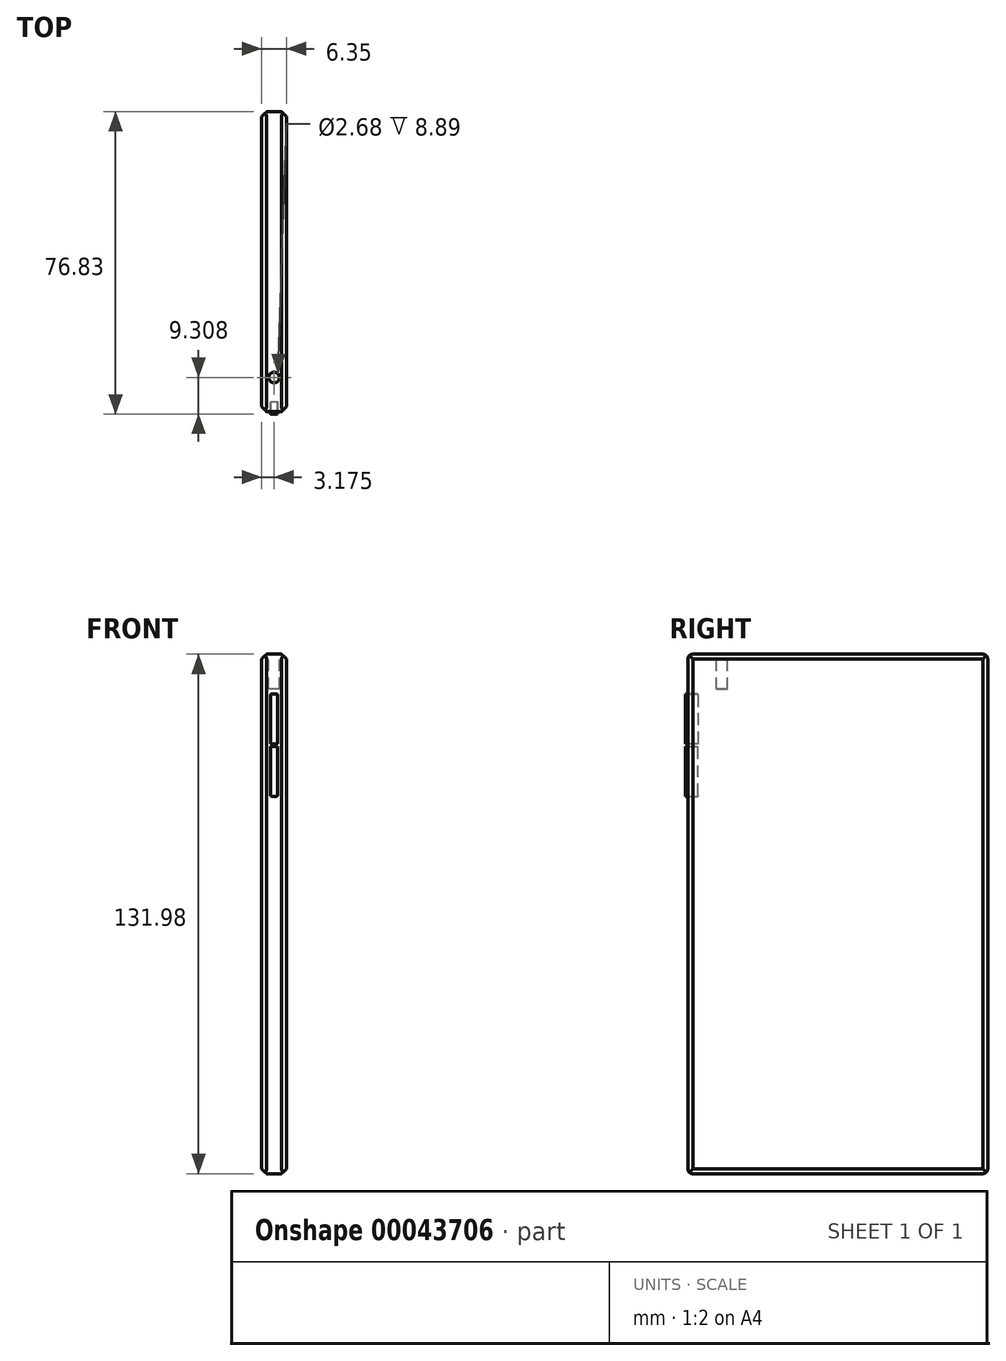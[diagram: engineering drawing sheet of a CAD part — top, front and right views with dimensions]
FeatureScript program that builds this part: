
annotation { "Feature Type Name" : "Feature", "Feature Type Description" : "" }
export const myFeature = defineFeature(function(context is Context, id is Id, definition is map)
    precondition{}
    {
        {
            var Q0;
            Q0=qCreatedBy(makeId("Right.planeOp"),FACE);
            var sketch = newSketch(context, id + "F0", { "sketchPlane" : qUnion([Q0])});
            skLineSegment(sketch, "E0.bottom", {"start": v(-38.1, -63.9) * mm, "end": v(38.1, -63.9) * mm});
            skLineSegment(sketch, "E0.top", {"start": v(-38.1, 68.08) * mm, "end": v(38.1, 68.08) * mm});
            skLineSegment(sketch, "E0.left", {"start": v(-38.1, -63.9) * mm, "end": v(-38.1, 68.08) * mm});
            skLineSegment(sketch, "E0.right", {"start": v(38.1, -63.9) * mm, "end": v(38.1, 68.08) * mm});
            skSolve(sketch);
        }
        {
            var Q0;
            Q0 = qSketchRegion(id + "F0", true);
            extrude(context, id + "F1", {"entities" : qUnion([Q0]), "depth" : 6.35 * mm});
        }
        {
            var Q0;
            Q0=makeQuery(id+"F1.opExtrude","CAP_FACE",FACE,{"disambiguationData":[OSD([sQuery(id+"F0.wireOp",EDGE,"E0.bottom"),sQuery(id+"F0.wireOp",EDGE,"E0.top"),sQuery(id+"F0.wireOp",EDGE,"E0.left"),sQuery(id+"F0.wireOp",EDGE,"E0.right")])],"isStart":false});
            var sketch = newSketch(context, id + "F2", { "sketchPlane" : qUnion([Q0])});
            skSolve(sketch);
        }
        {
            var Q0;
            Q0=makeQuery(id+"F1.opExtrude","CAP_EDGE",EDGE,{"disambiguationData":[OSD([sQuery(id+"F0.wireOp",EDGE,"E0.right")])],"isStart":false});
            var Q1;
            Q1=makeQuery(id+"F1.opExtrude","CAP_EDGE",EDGE,{"disambiguationData":[OSD([sQuery(id+"F0.wireOp",EDGE,"E0.right")])],"isStart":true});
            var Q2;
            Q2=makeQuery(id+"F1.opExtrude","CAP_EDGE",EDGE,{"disambiguationData":[OSD([sQuery(id+"F0.wireOp",EDGE,"E0.bottom")])],"isStart":false});
            var Q3;
            Q3=makeQuery(id+"F1.opExtrude","CAP_EDGE",EDGE,{"disambiguationData":[OSD([sQuery(id+"F0.wireOp",EDGE,"E0.bottom")])],"isStart":true});
            var Q4;
            Q4=makeQuery(id+"F1.opExtrude","CAP_EDGE",EDGE,{"disambiguationData":[OSD([sQuery(id+"F0.wireOp",EDGE,"E0.left")])],"isStart":false});
            var Q5;
            Q5=makeQuery(id+"F1.opExtrude","CAP_EDGE",EDGE,{"disambiguationData":[OSD([sQuery(id+"F0.wireOp",EDGE,"E0.left")])],"isStart":true});
            var Q6;
            Q6=makeQuery(id+"F1.opExtrude","CAP_EDGE",EDGE,{"disambiguationData":[OSD([sQuery(id+"F0.wireOp",EDGE,"E0.top")])],"isStart":false});
            var Q7;
            Q7=makeQuery(id+"F1.opExtrude","CAP_EDGE",EDGE,{"disambiguationData":[OSD([sQuery(id+"F0.wireOp",EDGE,"E0.top")])],"isStart":true});
            chamfer(context, id + "F3", {"entities" : qUnion([Q0, Q1, Q2, Q3, Q4, Q5, Q6, Q7]), "width" : 1.27 * mm, "tangentPropagation" : true});
        }
        {
            var Q0;
            Q0=makeQuery(id+"F1.opExtrude","SWEPT_EDGE",EDGE,{"disambiguationData":[OSD([sQuery(id+"F0.wireOp",EDGE,"E0.top"),sQuery(id+"F0.wireOp",EDGE,"E0.left")])]});
            var Q1;
            Q1=makeQuery(id+"F1.opExtrude","SWEPT_EDGE",EDGE,{"disambiguationData":[OSD([sQuery(id+"F0.wireOp",EDGE,"E0.bottom"),sQuery(id+"F0.wireOp",EDGE,"E0.left")])]});
            var Q2;
            Q2=makeQuery(id+"F1.opExtrude","SWEPT_EDGE",EDGE,{"disambiguationData":[OSD([sQuery(id+"F0.wireOp",EDGE,"E0.top"),sQuery(id+"F0.wireOp",EDGE,"E0.right")])]});
            var Q3;
            Q3=makeQuery(id+"F1.opExtrude","SWEPT_EDGE",EDGE,{"disambiguationData":[OSD([sQuery(id+"F0.wireOp",EDGE,"E0.bottom"),sQuery(id+"F0.wireOp",EDGE,"E0.right")])]});
            fillet(context, id + "F4", {"entities" : qUnion([Q0, Q1, Q2, Q3]), "radius" : 1.27 * mm, "tangentPropagation" : true, "allowEdgeOverflow" : false});
        }
        {
            var Q0;
            Q0=makeQuery(id+"F1.opExtrude","SWEPT_FACE",FACE,{"disambiguationData":[OSD([sQuery(id+"F0.wireOp",EDGE,"E0.left")])]});
            var sketch = newSketch(context, id + "F5", { "sketchPlane" : qUnion([Q0])});
            skLineSegment(sketch, "E1.bottom", {"start": v(2.54, 57.96) * mm, "end": v(3.8, 57.96) * mm});
            skLineSegment(sketch, "E1.top", {"start": v(2.54, 45.26) * mm, "end": v(3.81, 45.26) * mm});
            skLineSegment(sketch, "E1.left", {"start": v(2.29, 57.7) * mm, "end": v(2.29, 45.52) * mm});
            skLineSegment(sketch, "E1.right", {"start": v(4.06, 57.7) * mm, "end": v(4.06, 45.52) * mm});
            skLineSegment(sketch, "E2.MirrorCS", {"start": v(2.54, 44.68) * mm, "end": v(3.81, 44.68) * mm});
            skLineSegment(sketch, "E3.MirrorCS", {"start": v(2.29, 32.25) * mm, "end": v(2.29, 44.43) * mm});
            skLineSegment(sketch, "E4.MirrorCS", {"start": v(4.06, 32.25) * mm, "end": v(4.06, 44.43) * mm});
            skLineSegment(sketch, "E5.MirrorCS", {"start": v(2.54, 32) * mm, "end": v(3.8, 32) * mm});
            skPoint(sketch, "E6.visualSharp", {"position": v(2.29, 32) * mm});
            skArc(sketch, "E6.filletArc", {"start": v(2.29, 32.25) * mm, "mid": v(2.36, 32.07) * mm, "end": v(2.54, 32) * mm});
            skArc(sketch, "E7.filletArc", {"start": v(3.8, 32) * mm, "mid": v(3.99, 32.07) * mm, "end": v(4.06, 32.25) * mm});
            skPoint(sketch, "E8.visualSharp", {"position": v(2.29, 44.68) * mm});
            skArc(sketch, "E8.filletArc", {"start": v(2.54, 44.68) * mm, "mid": v(2.36, 44.6) * mm, "end": v(2.29, 44.43) * mm});
            skPoint(sketch, "E9.visualSharp", {"position": v(4.06, 44.68) * mm});
            skArc(sketch, "E9.filletArc", {"start": v(4.06, 44.43) * mm, "mid": v(3.99, 44.6) * mm, "end": v(3.81, 44.68) * mm});
            skPoint(sketch, "E10.visualSharp", {"position": v(2.29, 45.26) * mm});
            skArc(sketch, "E10.filletArc", {"start": v(2.29, 45.52) * mm, "mid": v(2.36, 45.34) * mm, "end": v(2.54, 45.26) * mm});
            skPoint(sketch, "E11.visualSharp", {"position": v(4.06, 45.26) * mm});
            skArc(sketch, "E11.filletArc", {"start": v(3.81, 45.26) * mm, "mid": v(3.99, 45.34) * mm, "end": v(4.06, 45.52) * mm});
            skPoint(sketch, "E12.visualSharp", {"position": v(2.29, 57.96) * mm});
            skArc(sketch, "E12.filletArc", {"start": v(2.54, 57.96) * mm, "mid": v(2.36, 57.89) * mm, "end": v(2.29, 57.7) * mm});
            skPoint(sketch, "E13.visualSharp", {"position": v(4.06, 57.96) * mm});
            skArc(sketch, "E13.filletArc", {"start": v(4.06, 57.7) * mm, "mid": v(3.99, 57.89) * mm, "end": v(3.8, 57.96) * mm});
            skSolve(sketch);
        }
        {
            var Q0;
            Q0=makeQuery(id+"F5.imprint","IMPRINT",FACE,{"disambiguationData":[TD([[makeQuery(id+"F5.imprint","IMPRINT",EDGE,{"derivedFrom":sQuery(id+"F5.wireOp",EDGE,"E1.bottom")}),-1.0]])]});
            var Q1;
            Q1=makeQuery(id+"F5.imprint","IMPRINT",FACE,{"disambiguationData":[TD([[makeQuery(id+"F5.imprint","IMPRINT",EDGE,{"derivedFrom":sQuery(id+"F5.wireOp",EDGE,"E2.MirrorCS")}),-1.0]])]});
            extrude(context, id + "F6", {"entities" : qUnion([Q0, Q1]), "operationType" : NewBodyOperationType.REMOVE, "oppositeDirection" : true, "depth" : 2.54 * mm});
        }
        {
            var Q0;
            Q0=makeQuery(id+"F1.opExtrude","SWEPT_FACE",FACE,{"disambiguationData":[OSD([sQuery(id+"F0.wireOp",EDGE,"E0.top")])]});
            var sketch = newSketch(context, id + "F7", { "sketchPlane" : qUnion([Q0])});
            skCircle(sketch, "E14", {"center": v(3.18, -29.42) * mm, "radius": 1.34 * mm});
            skSolve(sketch);
        }
        {
            var Q0;
            Q0 = qSketchRegion(id + "F7", true);
            extrude(context, id + "F8", {"entities" : qUnion([Q0]), "operationType" : NewBodyOperationType.REMOVE, "oppositeDirection" : true, "depth" : 8.9 * mm});
        }
        {
            var Q0;
            Q0=makeQuery(id+"F6.boolean.opBoolean","COPY",FACE,{"derivedFrom":makeQuery(id+"F6.opExtrude","CAP_FACE",FACE,{"disambiguationData":[OSD([sQuery(id+"F5.wireOp",EDGE,"E2.MirrorCS"),sQuery(id+"F5.wireOp",EDGE,"E3.MirrorCS"),sQuery(id+"F5.wireOp",EDGE,"E4.MirrorCS"),sQuery(id+"F5.wireOp",EDGE,"E5.MirrorCS"),sQuery(id+"F5.wireOp",EDGE,"E6.filletArc"),sQuery(id+"F5.wireOp",EDGE,"E7.filletArc"),sQuery(id+"F5.wireOp",EDGE,"E8.filletArc"),sQuery(id+"F5.wireOp",EDGE,"E9.filletArc")])],"isStart":false})});
            extrude(context, id + "F9", {"entities" : qUnion([Q0]), "depth" : 3.17 * mm});
        }
        {
            var Q0;
            Q0=makeQuery(id+"F6.boolean.opBoolean","COPY",FACE,{"derivedFrom":makeQuery(id+"F6.opExtrude","CAP_FACE",FACE,{"disambiguationData":[OSD([sQuery(id+"F5.wireOp",EDGE,"E1.bottom"),sQuery(id+"F5.wireOp",EDGE,"E1.top"),sQuery(id+"F5.wireOp",EDGE,"E1.left"),sQuery(id+"F5.wireOp",EDGE,"E1.right"),sQuery(id+"F5.wireOp",EDGE,"E10.filletArc"),sQuery(id+"F5.wireOp",EDGE,"E11.filletArc"),sQuery(id+"F5.wireOp",EDGE,"E12.filletArc"),sQuery(id+"F5.wireOp",EDGE,"E13.filletArc")])],"isStart":false})});
            var sketch = newSketch(context, id + "F10", { "sketchPlane" : qUnion([Q0])});
            skLineSegment(sketch, "E15.0", {"start": v(4.06, 57.7) * mm, "end": v(4.06, 45.52) * mm});
            skLineSegment(sketch, "E16.0.0", {"start": v(3.8, 57.96) * mm, "end": v(2.54, 57.96) * mm});
            skArc(sketch, "E16.0.1", {"start": v(2.54, 57.96) * mm, "mid": v(2.36, 57.89) * mm, "end": v(2.29, 57.7) * mm});
            skLineSegment(sketch, "E16.0.2", {"start": v(2.29, 57.7) * mm, "end": v(2.29, 45.52) * mm});
            skArc(sketch, "E16.0.3", {"start": v(2.29, 45.52) * mm, "mid": v(2.36, 45.34) * mm, "end": v(2.54, 45.26) * mm});
            skLineSegment(sketch, "E16.0.4", {"start": v(2.54, 45.26) * mm, "end": v(3.81, 45.26) * mm});
            skArc(sketch, "E16.0.5", {"start": v(3.81, 45.26) * mm, "mid": v(3.99, 45.34) * mm, "end": v(4.06, 45.52) * mm});
            skLineSegment(sketch, "E16.0.6", {"start": v(4.06, 45.52) * mm, "end": v(4.06, 57.7) * mm});
            skArc(sketch, "E16.0.7", {"start": v(4.06, 57.7) * mm, "mid": v(3.99, 57.89) * mm, "end": v(3.8, 57.96) * mm});
            skSolve(sketch);
        }
        {
            var Q0;
            Q0=makeQuery(id+"F10.imprint","IMPRINT",FACE,{"disambiguationData":[TD([[makeQuery(id+"F10.imprint","IMPRINT",EDGE,{"derivedFrom":sQuery(id+"F10.wireOp",EDGE,"E16.0.0")}),-1.0]])]});
            extrude(context, id + "F11", {"entities" : qUnion([Q0]), "depth" : 3.17 * mm});
        }
    });
